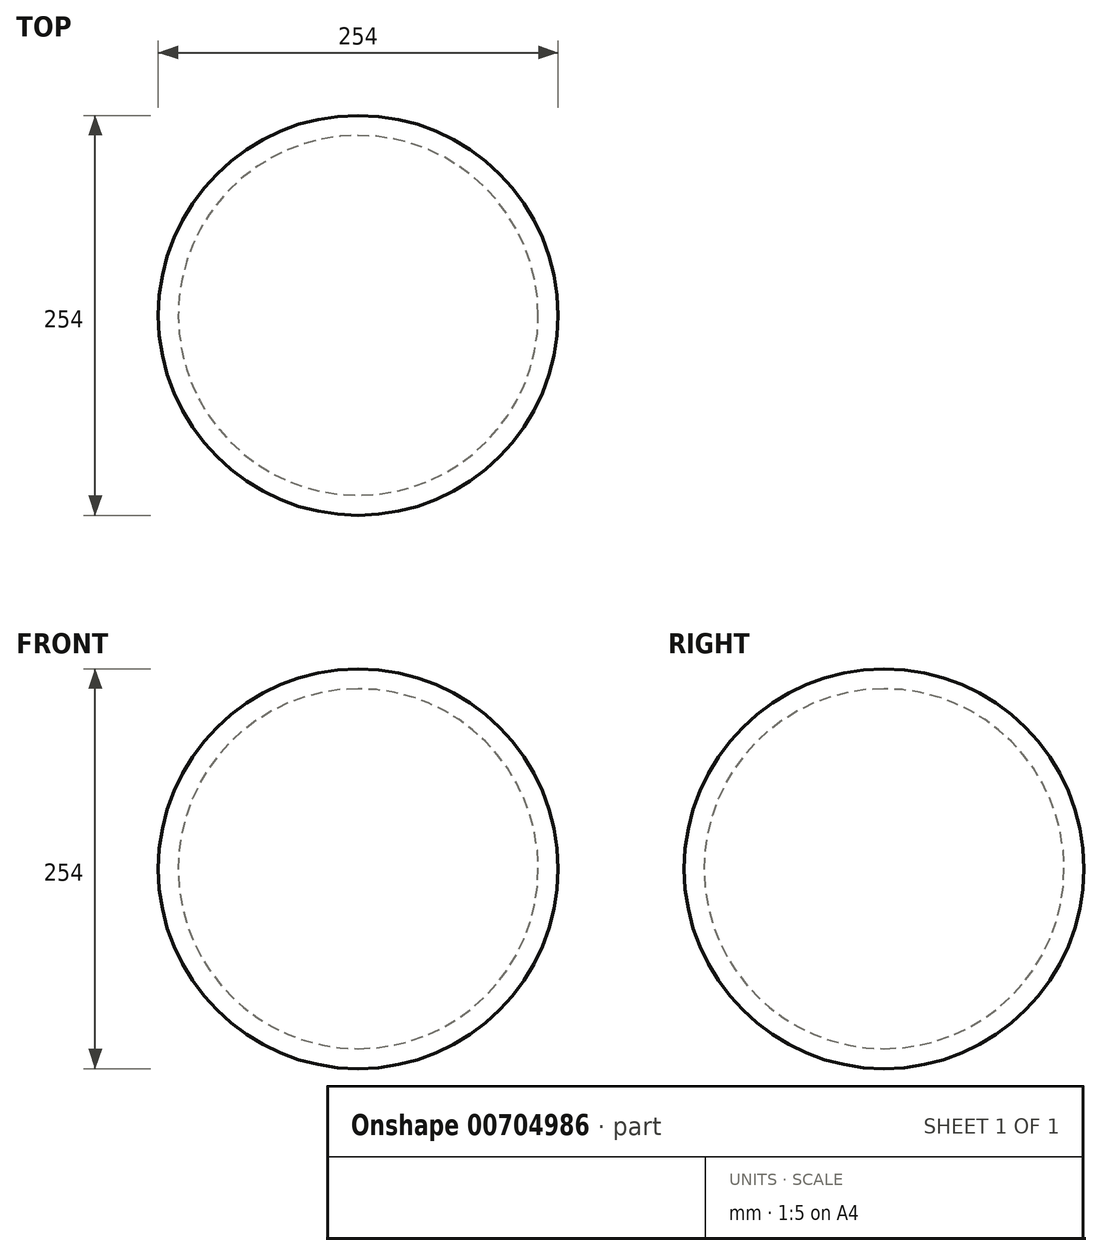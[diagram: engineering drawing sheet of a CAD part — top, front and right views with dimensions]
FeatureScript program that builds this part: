
annotation { "Feature Type Name" : "Feature", "Feature Type Description" : "" }
export const myFeature = defineFeature(function(context is Context, id is Id, definition is map)
    precondition{}
    {
        {
            var Q0;
            Q0=qCreatedBy(makeId("Front.planeOp"),FACE);
            var sketch = newSketch(context, id + "F0", { "sketchPlane" : qUnion([Q0])});
            skArc(sketch, "E0", {"start": v(0, 127) * mm, "mid": v(-127, 0) * mm, "end": v(0, -127) * mm});
            skArc(sketch, "E1", {"start": v(0, 114.3) * mm, "mid": v(-114.3, 0) * mm, "end": v(0, -114.3) * mm});
            skLineSegment(sketch, "E2.trimOffspring", {"start": v(0, -114.3) * mm, "end": v(0, -127) * mm});
            skLineSegment(sketch, "E3", {"start": v(0, 127) * mm, "end": v(0, 114.3) * mm});
            skSolve(sketch);
        }
        {
            var Q0;
            Q0=makeQuery(id+"F0.imprint","IMPRINT",FACE,{"disambiguationData":[TD([[makeQuery(id+"F0.imprint","IMPRINT",EDGE,{"derivedFrom":sQuery(id+"F0.wireOp",EDGE,"E0")}),1.0]])]});
            var Q1;
            Q1=sQuery(id+"F0.wireOp",EDGE,"E3");
            revolve(context, id + "F1", {"surfaceOperationType" : NewSurfaceOperationType.NEW, "entities" : qUnion([Q0]), "axis" : qUnion([Q1]), "revolveType" : RevolveType.FULL});
        }
    });
